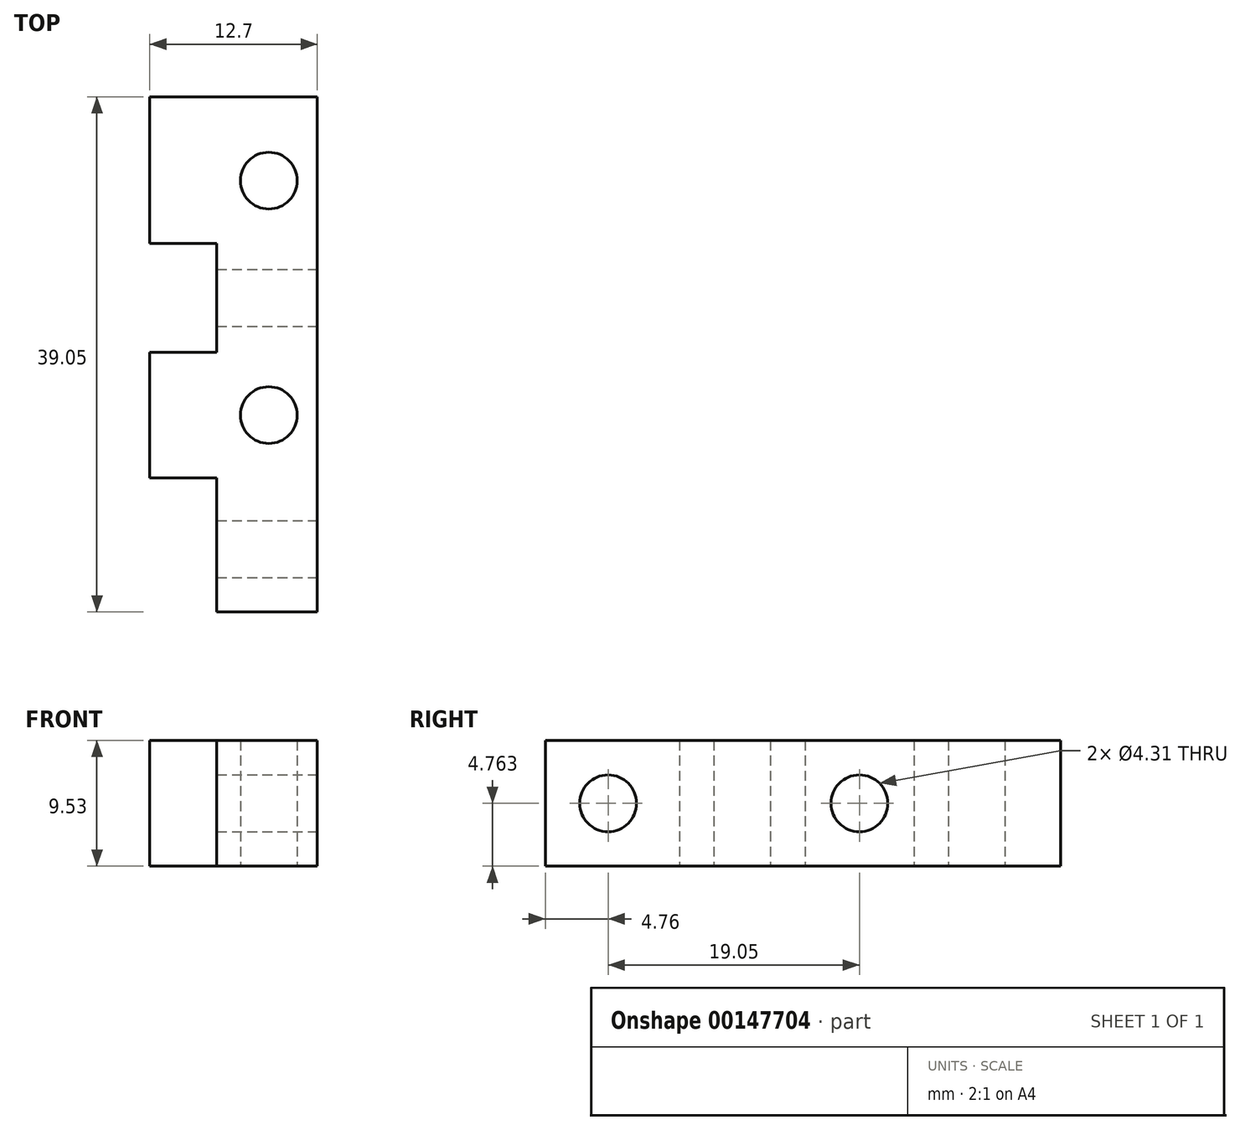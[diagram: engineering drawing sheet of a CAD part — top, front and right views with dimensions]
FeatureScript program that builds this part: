
annotation { "Feature Type Name" : "Feature", "Feature Type Description" : "" }
export const myFeature = defineFeature(function(context is Context, id is Id, definition is map)
    precondition{}
    {
        {
            var Q0;
            Q0=qCreatedBy(makeId("Top.planeOp"),FACE);
            var sketch = newSketch(context, id + "F0", { "sketchPlane" : qUnion([Q0])});
            skLineSegment(sketch, "E0.bottom", {"start": v(0, 0) * mm, "end": v(12.7, 0) * mm});
            skLineSegment(sketch, "E0.top", {"start": v(5.08, -39.05) * mm, "end": v(12.7, -39.05) * mm});
            skLineSegment(sketch, "E0.right", {"start": v(12.7, 0) * mm, "end": v(12.7, -39.05) * mm});
            skLineSegment(sketch, "E1", {"start": v(9.02, 0) * mm, "end": v(9.02, -6.35) * mm, "construction": true});
            skLineSegment(sketch, "E2", {"start": v(9.02, -6.35) * mm, "end": v(9.02, -24.13) * mm, "construction": true});
            skCircle(sketch, "E3", {"center": v(9.02, -6.35) * mm, "radius": 2.15 * mm});
            skCircle(sketch, "E4", {"center": v(9.02, -24.13) * mm, "radius": 2.15 * mm});
            skLineSegment(sketch, "E5", {"start": v(9.02, -24.13) * mm, "end": v(9.02, -39.05) * mm, "construction": true});
            skPoint(sketch, "E6", {"position": v(9.02, -15.24) * mm});
            skLineSegment(sketch, "E7", {"start": v(0, 0) * mm, "end": v(0, -11.11) * mm});
            skLineSegment(sketch, "E8", {"start": v(0, -11.11) * mm, "end": v(5.08, -11.11) * mm});
            skLineSegment(sketch, "E9", {"start": v(5.08, -11.11) * mm, "end": v(5.08, -19.37) * mm});
            skLineSegment(sketch, "E10", {"start": v(5.08, -19.37) * mm, "end": v(0, -19.37) * mm});
            skLineSegment(sketch, "E11", {"start": v(0, -19.37) * mm, "end": v(0, -28.9) * mm});
            skLineSegment(sketch, "E12", {"start": v(0, -28.9) * mm, "end": v(5.08, -28.9) * mm});
            skLineSegment(sketch, "E13", {"start": v(5.08, -28.9) * mm, "end": v(5.08, -39.05) * mm});
            skLineSegment(sketch, "E14", {"start": v(9.02, -6.35) * mm, "end": v(0, -6.35) * mm, "construction": true});
            skLineSegment(sketch, "E15", {"start": v(4.5, -11.11) * mm, "end": v(4.5, -6.35) * mm, "construction": true});
            skLineSegment(sketch, "E16", {"start": v(9.02, -24.13) * mm, "end": v(0, -24.13) * mm, "construction": true});
            skSolve(sketch);
        }
        {
            var Q0;
            Q0=qSketchRegion(id+"F0",true);
            extrude(context, id + "F1", {"entities" : qUnion([Q0]), "depth" : 9.52 * mm});
        }
        {
            var Q0;
            Q0=makeQuery(id+"F1.opExtrude","SWEPT_FACE",FACE,{"disambiguationData":[OSD([sQuery(id+"F0.wireOp",EDGE,"E0.right")])]});
            var sketch = newSketch(context, id + "F2", { "sketchPlane" : qUnion([Q0])});
            skLineSegment(sketch, "E17", {"start": v(-39.05, 4.76) * mm, "end": v(-34.3, 4.76) * mm, "construction": true});
            skLineSegment(sketch, "E18", {"start": v(-6.35, 4.76) * mm, "end": v(-24.13, 4.76) * mm, "construction": true});
            skLineSegment(sketch, "E19", {"start": v(-6.35, 4.76) * mm, "end": v(-6.35, 9.53) * mm, "construction": true});
            skLineSegment(sketch, "E20", {"start": v(-24.13, 4.76) * mm, "end": v(-24.13, 9.53) * mm, "construction": true});
            skCircle(sketch, "E21", {"center": v(-34.3, 4.76) * mm, "radius": 2.15 * mm});
            skCircle(sketch, "E22", {"center": v(-15.24, 4.76) * mm, "radius": 2.15 * mm});
            skSolve(sketch);
        }
        {
            var Q0;
            Q0=qSketchRegion(id+"F2",true);
            var Q1;
            Q1=makeQuery(id+"F1.opExtrude","SWEPT_FACE",FACE,{"disambiguationData":[OSD([sQuery(id+"F0.wireOp",EDGE,"E7")])]});
            extrude(context, id + "F3", {"entities" : qUnion([Q0]), "operationType" : NewBodyOperationType.REMOVE, "endBound" : BoundingType.UP_TO_SURFACE, "oppositeDirection" : true, "endBoundEntityFace" : qUnion([Q1]), "depth" : 25.4 * mm});
        }
    });
